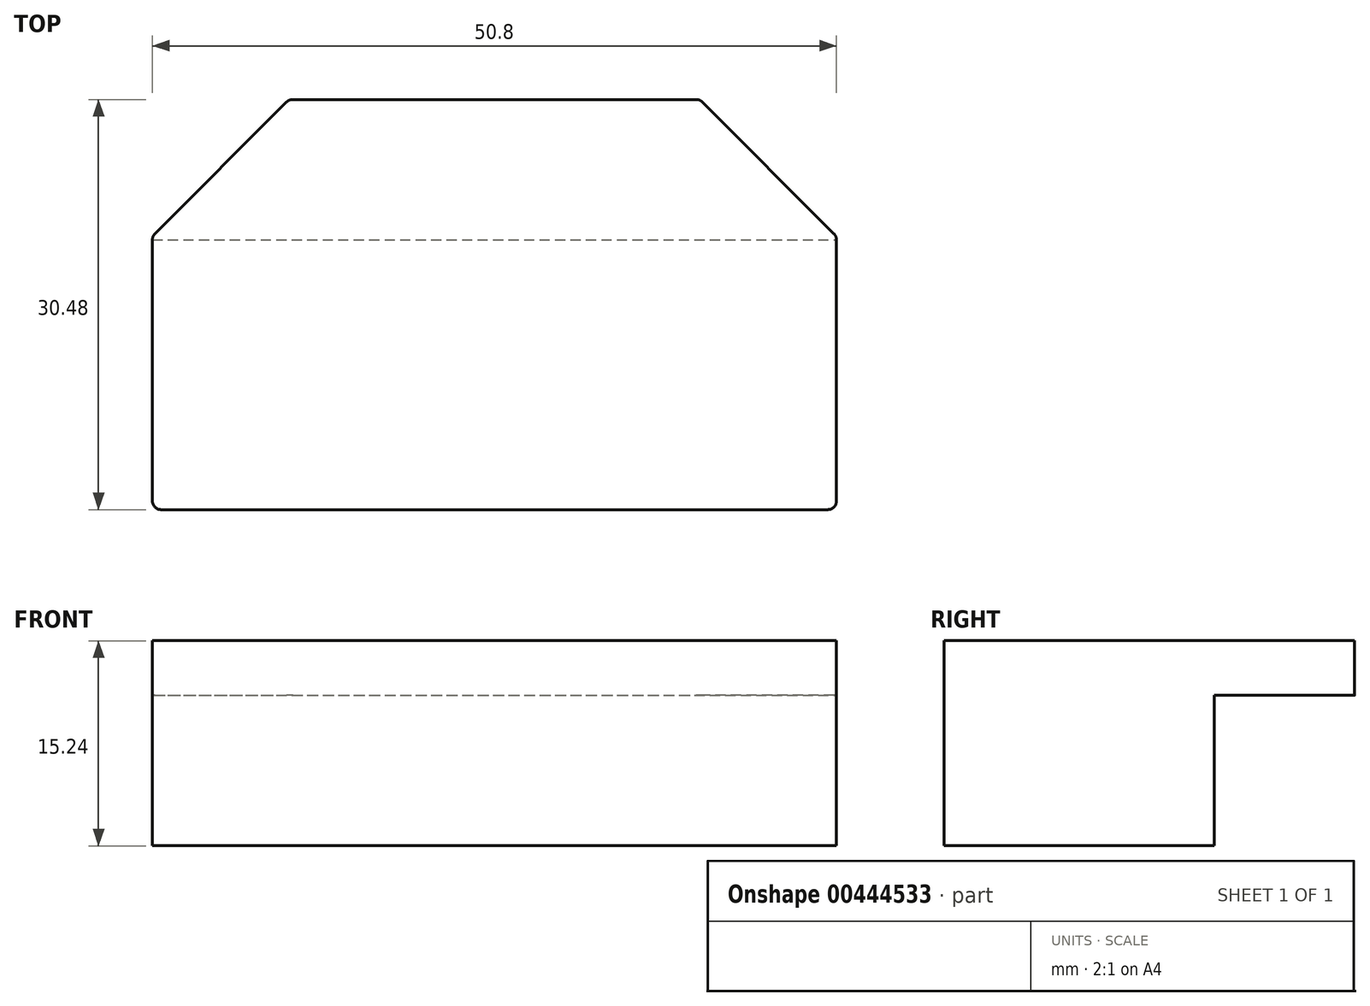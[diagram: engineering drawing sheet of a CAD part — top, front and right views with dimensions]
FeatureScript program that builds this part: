
annotation { "Feature Type Name" : "Feature", "Feature Type Description" : "" }
export const myFeature = defineFeature(function(context is Context, id is Id, definition is map)
    precondition{}
    {
        {
            var Q0;
            Q0=qCreatedBy(makeId("Top.planeOp"),FACE);
            var sketch = newSketch(context, id + "F0", { "sketchPlane" : qUnion([Q0])});
            skLineSegment(sketch, "E0", {"start": v(0, 46.25) * mm, "end": v(0, -48.37) * mm, "construction": true});
            skLineSegment(sketch, "E1.bottom", {"start": v(-14.98, 10.16) * mm, "end": v(14.98, 10.16) * mm});
            skLineSegment(sketch, "E1.top", {"start": v(-24.77, -20.32) * mm, "end": v(24.77, -20.32) * mm});
            skLineSegment(sketch, "E1.left", {"start": v(-25.4, -0.26) * mm, "end": v(-25.4, -1.25) * mm});
            skLineSegment(sketch, "E1.right", {"start": v(25.4, -0.26) * mm, "end": v(25.4, -19.69) * mm});
            skLineSegment(sketch, "E2", {"start": v(-15.24, 20.46) * mm, "end": v(-15.24, -30.04) * mm, "construction": true});
            skLineSegment(sketch, "E3", {"start": v(-25.21, 0.19) * mm, "end": v(-15.43, 9.97) * mm});
            skPoint(sketch, "E3.startSnap0", {"position": v(-25.4, -5.08) * mm});
            skLineSegment(sketch, "E4", {"start": v(-25.4, -1.25) * mm, "end": v(-25.4, -19.69) * mm});
            skPoint(sketch, "E5.orphan", {"position": v(-25.4, 10.16) * mm});
            skLineSegment(sketch, "E6.MirrorCS", {"start": v(-4.94, 10.16) * mm, "end": v(-55.44, 10.16) * mm, "construction": true});
            skLineSegment(sketch, "E7.MirrorCS", {"start": v(25.21, 0.19) * mm, "end": v(15.43, 9.97) * mm});
            skLineSegment(sketch, "E8", {"start": v(-55.1, 0) * mm, "end": v(41.54, 0) * mm, "construction": true});
            skPoint(sketch, "E9.visualSharp", {"position": v(15.24, 10.16) * mm});
            skArc(sketch, "E9.filletArc", {"start": v(15.43, 9.97) * mm, "mid": v(15.22, 10.11) * mm, "end": v(14.98, 10.16) * mm});
            skPoint(sketch, "E10.visualSharp", {"position": v(25.4, 0) * mm});
            skArc(sketch, "E10.filletArc", {"start": v(25.4, -0.26) * mm, "mid": v(25.35, -0.02) * mm, "end": v(25.21, 0.19) * mm});
            skPoint(sketch, "E11.visualSharp", {"position": v(25.4, -20.32) * mm});
            skArc(sketch, "E11.filletArc", {"start": v(24.77, -20.32) * mm, "mid": v(25.21, -20.13) * mm, "end": v(25.4, -19.69) * mm});
            skPoint(sketch, "E12.visualSharp", {"position": v(-25.4, -20.32) * mm});
            skArc(sketch, "E12.filletArc", {"start": v(-25.4, -19.69) * mm, "mid": v(-25.21, -20.13) * mm, "end": v(-24.77, -20.32) * mm});
            skPoint(sketch, "E13.visualSharp", {"position": v(-25.4, 0) * mm});
            skArc(sketch, "E13.filletArc", {"start": v(-25.21, 0.19) * mm, "mid": v(-25.35, -0.02) * mm, "end": v(-25.4, -0.26) * mm});
            skPoint(sketch, "E14.visualSharp", {"position": v(-15.24, 10.16) * mm});
            skArc(sketch, "E14.filletArc", {"start": v(-14.98, 10.16) * mm, "mid": v(-15.22, 10.11) * mm, "end": v(-15.43, 9.97) * mm});
            skSolve(sketch);
        }
        {
            var Q0;
            Q0 = qSketchRegion(id + "F0", true);
            extrude(context, id + "F1", {"entities" : qUnion([Q0]), "depth" : 4.06 * mm});
        }
        {
            var Q0;
            Q0=makeQuery(id+"F1.opExtrude","CAP_FACE",FACE,{"disambiguationData":[OSD([sQuery(id+"F0.wireOp",EDGE,"E1.bottom"),sQuery(id+"F0.wireOp",EDGE,"E1.top"),sQuery(id+"F0.wireOp",EDGE,"E1.left"),sQuery(id+"F0.wireOp",EDGE,"E1.right"),sQuery(id+"F0.wireOp",EDGE,"E3"),sQuery(id+"F0.wireOp",EDGE,"E4"),sQuery(id+"F0.wireOp",EDGE,"E7.MirrorCS"),sQuery(id+"F0.wireOp",EDGE,"E9.filletArc"),sQuery(id+"F0.wireOp",EDGE,"E10.filletArc"),sQuery(id+"F0.wireOp",EDGE,"E11.filletArc"),sQuery(id+"F0.wireOp",EDGE,"E12.filletArc"),sQuery(id+"F0.wireOp",EDGE,"E13.filletArc"),sQuery(id+"F0.wireOp",EDGE,"E14.filletArc")])],"isStart":false});
            var sketch = newSketch(context, id + "F2", { "sketchPlane" : qUnion([Q0])});
            skArc(sketch, "E15.0.0", {"start": v(-25.4, -19.69) * mm, "mid": v(-25.21, -20.13) * mm, "end": v(-24.77, -20.32) * mm});
            skLineSegment(sketch, "E15.0.1", {"start": v(-24.77, -20.32) * mm, "end": v(24.77, -20.32) * mm});
            skArc(sketch, "E15.0.2", {"start": v(24.77, -20.32) * mm, "mid": v(25.21, -20.13) * mm, "end": v(25.4, -19.69) * mm});
            skLineSegment(sketch, "E15.0.3", {"start": v(25.4, -19.69) * mm, "end": v(25.4, -0.26) * mm});
            skLineSegment(sketch, "E15.0.11", {"start": v(-25.4, -0.26) * mm, "end": v(-25.4, -19.69) * mm});
            skLineSegment(sketch, "E16", {"start": v(-25.4, -0.26) * mm, "end": v(25.4, -0.26) * mm});
            skPoint(sketch, "E15.0.10.start.orphan", {"position": v(-25.21, 0.19) * mm});
            skPoint(sketch, "E15.0.8.end.orphan", {"position": v(-15.43, 9.97) * mm});
            skPoint(sketch, "E15.0.8.start.orphan", {"position": v(-14.98, 10.16) * mm});
            skPoint(sketch, "E15.0.6.end.orphan", {"position": v(14.98, 10.16) * mm});
            skPoint(sketch, "E15.0.6.start.orphan", {"position": v(15.43, 9.97) * mm});
            skPoint(sketch, "E15.0.4.end.orphan", {"position": v(25.21, 0.19) * mm});
            skSolve(sketch);
        }
        {
            var Q0;
            Q0 = qSketchRegion(id + "F2", true);
            extrude(context, id + "F3", {"entities" : qUnion([Q0]), "operationType" : NewBodyOperationType.ADD, "oppositeDirection" : true, "depth" : 15.24 * mm});
        }
        {
            var Q0;
            Q0 = qSketchRegion(id + "F2", true);
            extrude(context, id + "F4", {"entities" : qUnion([Q0]), "operationType" : NewBodyOperationType.ADD, "oppositeDirection" : true, "depth" : 15.24 * mm});
        }
    });
